# Revit family: RLC6SL
name_source: partatom
category: Lighting Fixtures
revit_build: Autodesk Revit 2014 (Build: 20130308_1515(x64)
units: mm (PartAtom-declared; Revit-internal decimal feet)

## types (1)
- RLC6
    Apparent Load = 0 VA
    Application = Education,Healthcare,Hospitality,Office,Lobby,Conference Room,Classroom,Waiting Room,Auditorium,Guest Room,Dining Area
    Color Filter = 16777215
    Default Elevation = 48"
    Description = Retroficient is designed specifically to retrofit into ceilings with existing recessed downlight fixtures
    Dimming Lamp Color Temperature Shift = <None>
    Emit Shape Visible in Rendering = No
    Emit from Circle Diameter = 6"
    Housing = Hubbell - Steel
    Input Watts = 17 W
    Lamp = LED
    Load Classification = Lighting
    Manufacturer = Prescolite
    Model = RLC6SL
    Photometric Web File = RLC6SL_6LCSL10L35K8.ies
    Photometric Web Link = https://www.hubbell.com
    Product Documentation Link = https://hubbellcdn.com
    Product Page URL = https://www.hubbell.com
    Reflector = Hubbell - Aluminum
    Tilt Angle = -90.00°
    URL = https://www.hubbell.com
    Voltage = 120 V
    Wattage Comments = 17W - 42W

## geometry (parser evidence)
native form markers: Blend x6, Sweep x1
no freeform markers — native parametric forms only
